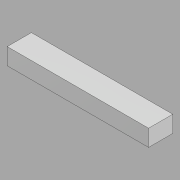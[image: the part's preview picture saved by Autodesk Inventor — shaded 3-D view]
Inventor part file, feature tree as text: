
AUTODESK INVENTOR PART (.ipt)
format: ipt  version: 2022.2 (Build 262287010, 287A)  size: 105,984 bytes
history: native  units: in
note: dims shown in document units (in); Inventor stores cm internally (conversion verified against a paired STEP export)
features: direct_edit x1, other x1, revolve x1
ambient origin geometry x8: Origin, YZ Plane, XZ Plane, XY Plane, X Axis, Y Axis, Z Axis, Center Point
bodies: Solid1 (feature_tree)
feature tree (3):
  direct_edit  "Direct Edit1"
  other  "L Vert rect jamb upper (1)"
  revolve  "Rotate1"  Angle=90.0deg
